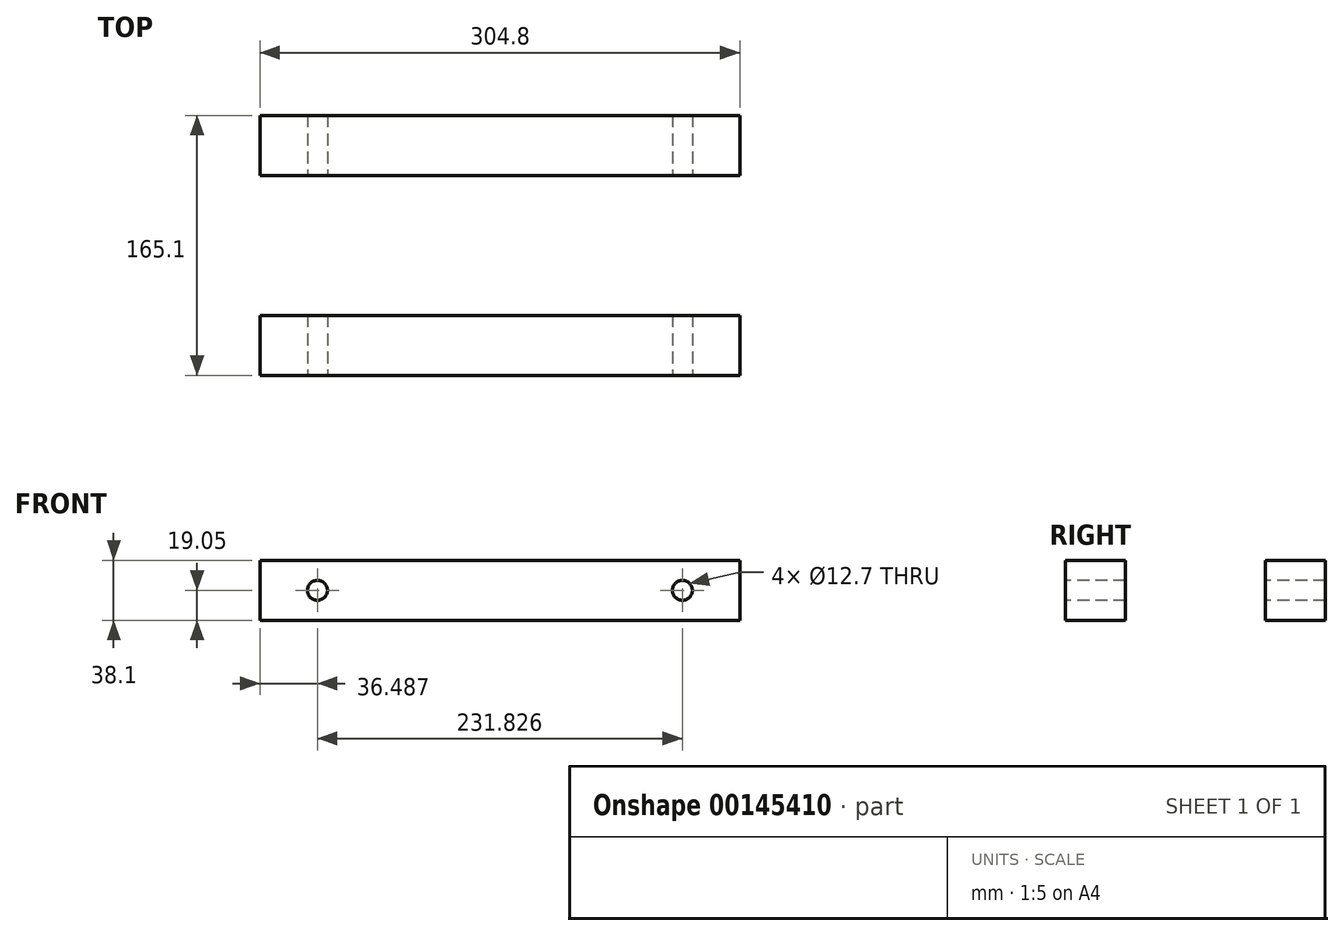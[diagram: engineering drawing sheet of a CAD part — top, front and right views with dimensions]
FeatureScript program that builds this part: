
annotation { "Feature Type Name" : "Feature", "Feature Type Description" : "" }
export const myFeature = defineFeature(function(context is Context, id is Id, definition is map)
    precondition{}
    {
        {
            var Q0;
            Q0=qCreatedBy(makeId("Front.planeOp"),FACE);
            var sketch = newSketch(context, id + "F0", { "sketchPlane" : qUnion([Q0])});
            skLineSegment(sketch, "E0.bottom", {"start": v(-152.4, 19.05) * mm, "end": v(152.4, 19.05) * mm});
            skLineSegment(sketch, "E0.top", {"start": v(-152.4, -19.05) * mm, "end": v(152.4, -19.05) * mm});
            skLineSegment(sketch, "E0.left", {"start": v(-152.4, 19.05) * mm, "end": v(-152.4, -19.05) * mm});
            skLineSegment(sketch, "E0.right", {"start": v(152.4, 19.05) * mm, "end": v(152.4, -19.05) * mm});
            skPoint(sketch, "E0.middle", {"position": v(0, 0) * mm});
            skSolve(sketch);
        }
        {
            var Q0;
            Q0 = qSketchRegion(id + "F0", true);
            extrude(context, id + "F1", {"entities" : qUnion([Q0]), "endBound" : BoundingType.SYMMETRIC, "depth" : 38.1 * mm});
        }
        {
            var Q0;
            Q0=makeQuery(id+"F1.opExtrude","SWEPT_BODY",BODY,{"disambiguationData":[OSD([sQuery(id+"F0.wireOp",EDGE,"E0.bottom"),sQuery(id+"F0.wireOp",EDGE,"E0.top"),sQuery(id+"F0.wireOp",EDGE,"E0.left"),sQuery(id+"F0.wireOp",EDGE,"E0.right")])]});
            transform(context, id + "F2", {"entities" : qUnion([Q0]), "transformType" : TransformType.TRANSLATION_3D, "dx" : 0 * mm, "dy" : 127 * mm, "dz" : 0 * mm, "makeCopy" : true});
        }
        {
            var Q0;
            Q0=qCreatedBy(makeId("Front.planeOp"),FACE);
            cPlane(context, id + "F3", {"entities" : qUnion([Q0]), "cplaneType" : CPlaneType.OFFSET, "offset" : 91.44 * mm, "width" : 152.4 * mm, "height" : 152.4 * mm});
        }
        {
            var Q0;
            Q0=qCreatedBy(id+"F3.planeOp",FACE);
            var sketch = newSketch(context, id + "F4", { "sketchPlane" : qUnion([Q0])});
            skPoint(sketch, "E1", {"position": v(115.91, 0) * mm});
            skPoint(sketch, "E2", {"position": v(-115.91, 0) * mm});
            skSolve(sketch);
        }
        {
            var Q0;
            Q0=sQuery(id+"F4.wireOp",VERTEX,"E1");
            var Q1;
            Q1=makeQuery(id+"F1.opExtrude","SWEPT_BODY",BODY,{"disambiguationData":[OSD([sQuery(id+"F0.wireOp",EDGE,"E0.bottom"),sQuery(id+"F0.wireOp",EDGE,"E0.top"),sQuery(id+"F0.wireOp",EDGE,"E0.left"),sQuery(id+"F0.wireOp",EDGE,"E0.right")])]});
            var Q2;
            Q2=makeQuery(id+"F2.opPattern","COPY",BODY,{"derivedFrom":makeQuery(id+"F1.opExtrude","SWEPT_BODY",BODY,{"disambiguationData":[OSD([sQuery(id+"F0.wireOp",EDGE,"E0.bottom"),sQuery(id+"F0.wireOp",EDGE,"E0.top"),sQuery(id+"F0.wireOp",EDGE,"E0.left"),sQuery(id+"F0.wireOp",EDGE,"E0.right")])]}),"instanceName":"1"});
            hole(context, id + "F5", {"style" : HoleStyle.SIMPLE, "endStyle" : HoleEndStyle.BLIND, "holeDiameter" : 12.7 * mm, "holeDepth" : 609.6 * mm, "startFromSketch" : true, "locations" : qUnion([Q0]), "scope" : qUnion([Q1, Q2])});
        }
        {
            var Q0;
            Q0=sQuery(id+"F4.wireOp",VERTEX,"E2");
            var Q1;
            Q1=makeQuery(id+"F1.opExtrude","SWEPT_BODY",BODY,{"disambiguationData":[OSD([sQuery(id+"F0.wireOp",EDGE,"E0.bottom"),sQuery(id+"F0.wireOp",EDGE,"E0.top"),sQuery(id+"F0.wireOp",EDGE,"E0.left"),sQuery(id+"F0.wireOp",EDGE,"E0.right")])]});
            var Q2;
            Q2=makeQuery(id+"F2.opPattern","COPY",BODY,{"derivedFrom":makeQuery(id+"F1.opExtrude","SWEPT_BODY",BODY,{"disambiguationData":[OSD([sQuery(id+"F0.wireOp",EDGE,"E0.bottom"),sQuery(id+"F0.wireOp",EDGE,"E0.top"),sQuery(id+"F0.wireOp",EDGE,"E0.left"),sQuery(id+"F0.wireOp",EDGE,"E0.right")])]}),"instanceName":"1"});
            hole(context, id + "F6", {"style" : HoleStyle.SIMPLE, "endStyle" : HoleEndStyle.BLIND, "holeDiameter" : 12.7 * mm, "holeDepth" : 609.6 * mm, "startFromSketch" : true, "locations" : qUnion([Q0]), "scope" : qUnion([Q1, Q2])});
        }
    });
